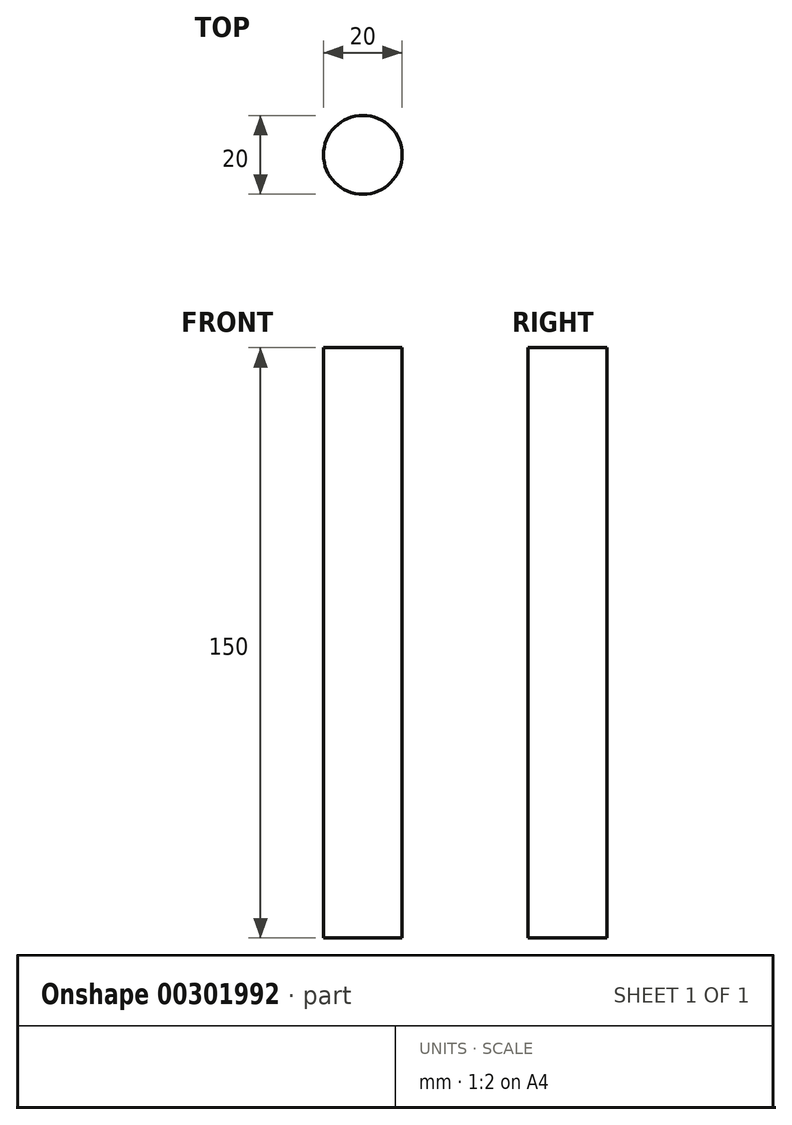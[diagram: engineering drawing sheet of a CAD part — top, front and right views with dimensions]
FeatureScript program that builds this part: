
annotation { "Feature Type Name" : "Feature", "Feature Type Description" : "" }
export const myFeature = defineFeature(function(context is Context, id is Id, definition is map)
    precondition{}
    {
        {
            var Q0;
            Q0=qCreatedBy(makeId("Top.planeOp"),FACE);
            var sketch = newSketch(context, id + "F0", { "sketchPlane" : qUnion([Q0])});
            skCircle(sketch, "E0", {"center": v(0, 0) * mm, "radius": 10 * mm});
            skSolve(sketch);
        }
        {
            var Q0;
            Q0=makeQuery(id+"F0.imprint","IMPRINT",FACE,{"disambiguationData":[TD([[makeQuery(id+"F0.imprint","IMPRINT",EDGE,{"derivedFrom":sQuery(id+"F0.wireOp",EDGE,"E0")}),1.0]])]});
            extrude(context, id + "F1", {"entities" : qUnion([Q0]), "depth" : 150 * mm});
        }
    });
